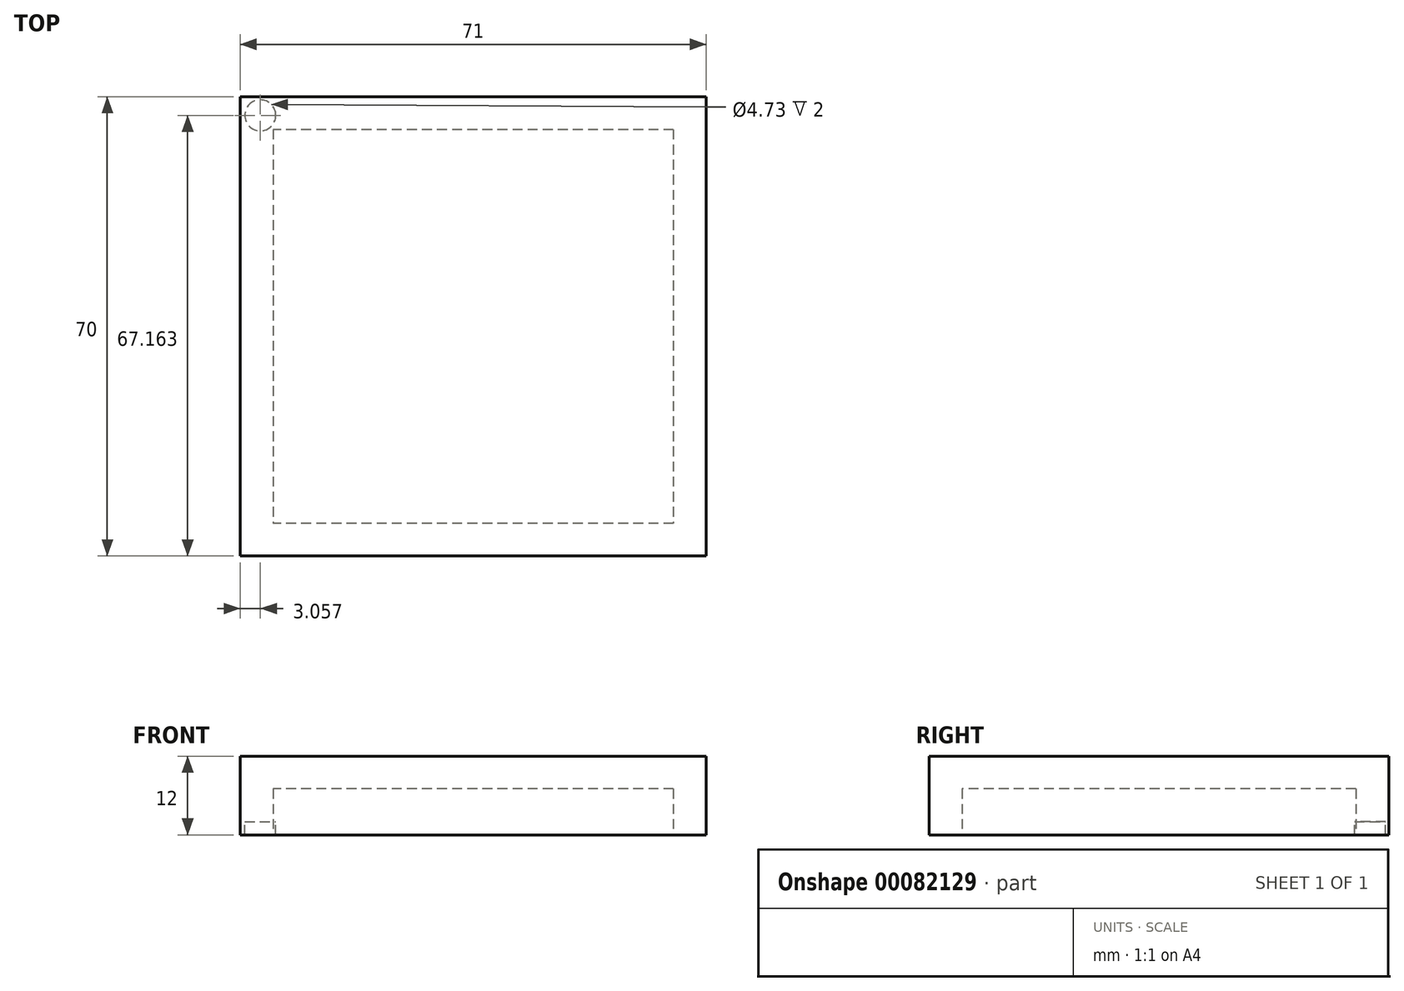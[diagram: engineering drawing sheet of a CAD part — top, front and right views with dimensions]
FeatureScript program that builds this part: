
annotation { "Feature Type Name" : "Feature", "Feature Type Description" : "" }
export const myFeature = defineFeature(function(context is Context, id is Id, definition is map)
    precondition{}
    {
        {
            var Q0;
            Q0=qCreatedBy(makeId("Top.planeOp"),FACE);
            var sketch = newSketch(context, id + "F0", { "sketchPlane" : qUnion([Q0])});
            skLineSegment(sketch, "E0.bottom", {"start": v(35.5, 35) * mm, "end": v(-35.5, 35) * mm});
            skLineSegment(sketch, "E0.top", {"start": v(35.5, -35) * mm, "end": v(-35.5, -35) * mm});
            skLineSegment(sketch, "E0.left", {"start": v(35.5, 35) * mm, "end": v(35.5, -35) * mm});
            skLineSegment(sketch, "E0.right", {"start": v(-35.5, 35) * mm, "end": v(-35.5, -35) * mm});
            skPoint(sketch, "E0.middle", {"position": v(0, 0) * mm});
            skSolve(sketch);
        }
        {
            var Q0;
            Q0=makeQuery(id+"F0.imprint","IMPRINT",FACE,{"disambiguationData":[TD([[makeQuery(id+"F0.imprint","IMPRINT",EDGE,{"derivedFrom":sQuery(id+"F0.wireOp",EDGE,"E0.bottom")}),1.0]])]});
            extrude(context, id + "F1", {"entities" : qUnion([Q0]), "depth" : 10 * mm});
        }
        {
            var Q0;
            Q0=makeQuery(id+"F1.opExtrude","CAP_FACE",FACE,{"disambiguationData":[OSD([sQuery(id+"F0.wireOp",EDGE,"E0.bottom"),sQuery(id+"F0.wireOp",EDGE,"E0.top"),sQuery(id+"F0.wireOp",EDGE,"E0.left"),sQuery(id+"F0.wireOp",EDGE,"E0.right")])],"isStart":true});
            shell(context, id + "F2", {"entities" : qUnion([Q0]), "thickness" : 5 * mm});
        }
        {
            var Q0;
            Q0=makeQuery(id+"F1.opExtrude","CAP_FACE",FACE,{"disambiguationData":[OSD([sQuery(id+"F0.wireOp",EDGE,"E0.bottom"),sQuery(id+"F0.wireOp",EDGE,"E0.top"),sQuery(id+"F0.wireOp",EDGE,"E0.left"),sQuery(id+"F0.wireOp",EDGE,"E0.right")])],"isStart":true});
            var sketch = newSketch(context, id + "F3", { "sketchPlane" : qUnion([Q0])});
            skCircle(sketch, "E1", {"center": v(-32.44, 32.16) * mm, "radius": 2.36 * mm});
            skSolve(sketch);
        }
        {
            var Q0;
            Q0=qCreatedBy(makeId("Top.planeOp"),FACE);
            var sketch = newSketch(context, id + "F4", { "sketchPlane" : qUnion([Q0])});
            skLineSegment(sketch, "E2", {"start": v(0, -37.33) * mm, "end": v(0, -32.62) * mm});
            skCircle(sketch, "E3.0", {"center": v(-32.44, -32.16) * mm, "radius": 2.36 * mm});
            skCircle(sketch, "E4.MirrorC", {"center": v(32.44, -32.16) * mm, "radius": 2.36 * mm});
            skSolve(sketch);
        }
        {
            var Q0;
            Q0=makeQuery(id+"F3.imprint","IMPRINT",FACE,{"disambiguationData":[TD([[makeQuery(id+"F3.imprint","IMPRINT",EDGE,{"derivedFrom":sQuery(id+"F3.wireOp",EDGE,"E1")}),-1.0]])]});
            var sketch = newSketch(context, id + "F5", { "sketchPlane" : qUnion([Q0])});
            skLineSegment(sketch, "E5", {"start": v(-31.6, 0) * mm, "end": v(-36.35, 0) * mm});
            skCircle(sketch, "E6.0", {"center": v(-32.44, 32.16) * mm, "radius": 2.36 * mm});
            skCircle(sketch, "E7.MirrorC", {"center": v(-32.44, -32.16) * mm, "radius": 2.36 * mm});
            skSolve(sketch);
        }
        {
            var Q0;
            Q0=makeQuery(id+"F3.imprint","IMPRINT",FACE,{"disambiguationData":[TD([[makeQuery(id+"F3.imprint","IMPRINT",EDGE,{"derivedFrom":sQuery(id+"F3.wireOp",EDGE,"E1")}),-1.0]])]});
            var sketch = newSketch(context, id + "F6", { "sketchPlane" : qUnion([Q0])});
            skLineSegment(sketch, "E8", {"start": v(36.09, 0) * mm, "end": v(32.09, 0) * mm});
            skCircle(sketch, "E9.0", {"center": v(32.44, 32.16) * mm, "radius": 2.36 * mm});
            skCircle(sketch, "E10.MirrorC", {"center": v(32.44, -32.16) * mm, "radius": 2.36 * mm});
            skSolve(sketch);
        }
        {
            var Q0;
            Q0=makeQuery(id+"F3.imprint","IMPRINT",FACE,{"disambiguationData":[TD([[makeQuery(id+"F3.imprint","IMPRINT",EDGE,{"derivedFrom":sQuery(id+"F3.wireOp",EDGE,"E1")}),1.0]])]});
            var Q1;
            Q1=makeQuery(id+"F4.imprint","IMPRINT",FACE,{"disambiguationData":[TD([[makeQuery(id+"F4.imprint","IMPRINT",EDGE,{"derivedFrom":sQuery(id+"F4.wireOp",EDGE,"E4.MirrorC")}),1.0]])]});
            extrude(context, id + "F7", {"entities" : qUnion([Q0, Q1]), "operationType" : NewBodyOperationType.ADD, "depth" : 2 * mm});
        }
        {
            var Q0;
            Q0=makeQuery(id+"F5.imprint","IMPRINT",FACE,{"disambiguationData":[TD([[makeQuery(id+"F5.imprint","IMPRINT",EDGE,{"derivedFrom":sQuery(id+"F5.wireOp",EDGE,"E7.MirrorC")}),-1.0]])]});
            var Q1;
            Q1=makeQuery(id+"F6.imprint","IMPRINT",FACE,{"disambiguationData":[TD([[makeQuery(id+"F6.imprint","IMPRINT",EDGE,{"derivedFrom":sQuery(id+"F6.wireOp",EDGE,"E10.MirrorC")}),1.0]])]});
            extrude(context, id + "F8", {"entities" : qUnion([Q0, Q1]), "operationType" : NewBodyOperationType.ADD, "depth" : 2 * mm});
        }
    });
